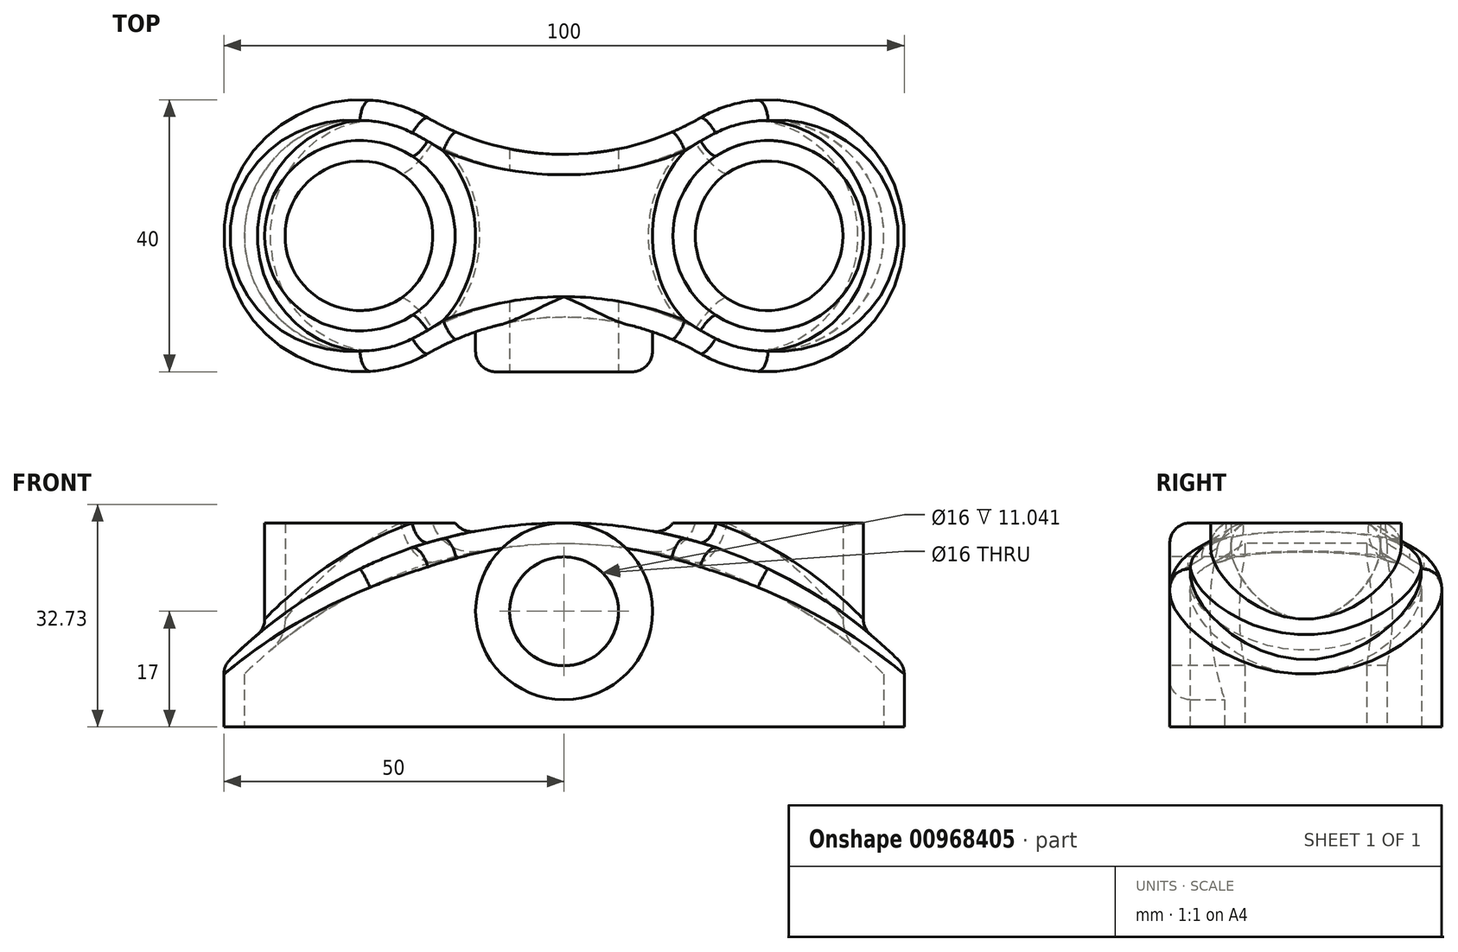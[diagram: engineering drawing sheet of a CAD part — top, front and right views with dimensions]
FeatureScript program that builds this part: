
annotation { "Feature Type Name" : "Feature", "Feature Type Description" : "" }
export const myFeature = defineFeature(function(context is Context, id is Id, definition is map)
    precondition{}
    {
        {
            var Q0;
            Q0=qCreatedBy(makeId("Top.planeOp"),FACE);
            var sketch = newSketch(context, id + "F0", { "sketchPlane" : qUnion([Q0])});
            skArc(sketch, "E0", {"start": v(-20, 17.32) * mm, "mid": v(-50, 0) * mm, "end": v(-20, -17.32) * mm});
            skArc(sketch, "E1", {"start": v(20, -17.32) * mm, "mid": v(50, 0) * mm, "end": v(20, 17.32) * mm});
            skArc(sketch, "E2", {"start": v(-20, 17.32) * mm, "mid": v(0, 11.96) * mm, "end": v(20, 17.32) * mm});
            skArc(sketch, "E3.MirrorCS", {"start": v(-20, -17.32) * mm, "mid": v(0, -11.96) * mm, "end": v(20, -17.32) * mm});
            skCircle(sketch, "E4", {"center": v(-30, 0) * mm, "radius": 11 * mm});
            skCircle(sketch, "E5", {"center": v(30, 0) * mm, "radius": 11 * mm});
            skCircle(sketch, "E6", {"center": v(-30, 0) * mm, "radius": 14 * mm});
            skCircle(sketch, "E7", {"center": v(30, 0) * mm, "radius": 14 * mm});
            skSolve(sketch);
        }
        {
            var Q0;
            Q0=qCreatedBy(makeId("Front.planeOp"),FACE);
            var sketch = newSketch(context, id + "F1", { "sketchPlane" : qUnion([Q0])});
            skCircle(sketch, "E8", {"center": v(0, 17) * mm, "radius": 13 * mm});
            skCircle(sketch, "E9", {"center": v(0, 17) * mm, "radius": 8 * mm});
            skSolve(sketch);
        }
        {
            var Q0;
            Q0=qCreatedBy(makeId("Front.planeOp"),FACE);
            var sketch = newSketch(context, id + "F2", { "sketchPlane" : qUnion([Q0])});
            skArc(sketch, "E10", {"start": v(57.45, 0) * mm, "mid": v(0, 30) * mm, "end": v(-57.45, 0) * mm});
            skSolve(sketch);
        }
        {
            var Q0;
            Q0=sQuery(id+"F2.wireOp",EDGE,"E10");
            extrude(context, id + "F3", {"bodyType" : ToolBodyType.SURFACE, "surfaceEntities" : qUnion([Q0]), "depth" : 50 * mm, "offsetDistance" : 25 * mm, "symmetric" : true});
        }
        {
            var Q0;
            Q0=makeQuery(id+"F0.imprint","IMPRINT",FACE,{"disambiguationData":[TD([[makeQuery(id+"F0.imprint","IMPRINT",EDGE,{"derivedFrom":sQuery(id+"F0.wireOp",EDGE,"E0")}),1.0]])]});
            var Q1;
            Q1=makeQuery(id+"F0.imprint","IMPRINT",FACE,{"disambiguationData":[TD([[makeQuery(id+"F0.imprint","IMPRINT",EDGE,{"derivedFrom":sQuery(id+"F0.wireOp",EDGE,"E4")}),-1.0]])]});
            var Q2;
            Q2=makeQuery(id+"F0.imprint","IMPRINT",FACE,{"disambiguationData":[TD([[makeQuery(id+"F0.imprint","IMPRINT",EDGE,{"derivedFrom":sQuery(id+"F0.wireOp",EDGE,"E4")}),1.0]])]});
            var Q3;
            Q3=makeQuery(id+"F0.imprint","IMPRINT",FACE,{"disambiguationData":[TD([[makeQuery(id+"F0.imprint","IMPRINT",EDGE,{"derivedFrom":sQuery(id+"F0.wireOp",EDGE,"E5")}),1.0]])]});
            var Q4;
            Q4=makeQuery(id+"F0.imprint","IMPRINT",FACE,{"disambiguationData":[TD([[makeQuery(id+"F0.imprint","IMPRINT",EDGE,{"derivedFrom":sQuery(id+"F0.wireOp",EDGE,"E5")}),-1.0]])]});
            var Q5;
            Q5=makeQuery(id+"F3.opExtrude","SWEPT_BODY",BODY,{"disambiguationData":[OSD([sQuery(id+"F2.wireOp",EDGE,"E10")])]});
            extrude(context, id + "F4", {"entities" : qUnion([Q0, Q1, Q2, Q3, Q4]), "endBound" : BoundingType.UP_TO_BODY, "depth" : 25 * mm, "endBoundEntityBody" : qUnion([Q5]), "offsetDistance" : 25 * mm});
        }
        {
            var Q0;
            Q0=makeQuery(id+"F0.imprint","IMPRINT",FACE,{"disambiguationData":[TD([[makeQuery(id+"F0.imprint","IMPRINT",EDGE,{"derivedFrom":sQuery(id+"F0.wireOp",EDGE,"E4")}),-1.0]])]});
            var Q1;
            Q1=makeQuery(id+"F0.imprint","IMPRINT",FACE,{"disambiguationData":[TD([[makeQuery(id+"F0.imprint","IMPRINT",EDGE,{"derivedFrom":sQuery(id+"F0.wireOp",EDGE,"E4")}),1.0]])]});
            var Q2;
            Q2=makeQuery(id+"F0.imprint","IMPRINT",FACE,{"disambiguationData":[TD([[makeQuery(id+"F0.imprint","IMPRINT",EDGE,{"derivedFrom":sQuery(id+"F0.wireOp",EDGE,"E5")}),-1.0]])]});
            var Q3;
            Q3=makeQuery(id+"F0.imprint","IMPRINT",FACE,{"disambiguationData":[TD([[makeQuery(id+"F0.imprint","IMPRINT",EDGE,{"derivedFrom":sQuery(id+"F0.wireOp",EDGE,"E5")}),1.0]])]});
            extrude(context, id + "F5", {"entities" : qUnion([Q0, Q1, Q2, Q3]), "operationType" : NewBodyOperationType.ADD, "depth" : 30 * mm, "offsetDistance" : 25 * mm});
        }
        {
            var Q0;
            Q0=makeQuery(id+"F5.boolean.opBoolean","INTERSECT",EDGE,{"derivedFrom":[makeQuery(id+"F4.opExtrude","CAP_FACE",FACE,{"disambiguationData":[OSD([sQuery(id+"F0.wireOp",EDGE,"E0"),sQuery(id+"F0.wireOp",EDGE,"E1"),sQuery(id+"F0.wireOp",EDGE,"E2"),sQuery(id+"F0.wireOp",EDGE,"E3.MirrorCS")])],"isStart":false}),makeQuery(id+"F5.opExtrude","SWEPT_FACE",FACE,{"disambiguationData":[OSD([sQuery(id+"F0.wireOp",EDGE,"E6")])]})]});
            var Q1;
            Q1=makeQuery(id+"F5.boolean.opBoolean","INTERSECT",EDGE,{"derivedFrom":[makeQuery(id+"F4.opExtrude","CAP_FACE",FACE,{"disambiguationData":[OSD([sQuery(id+"F0.wireOp",EDGE,"E0"),sQuery(id+"F0.wireOp",EDGE,"E1"),sQuery(id+"F0.wireOp",EDGE,"E2"),sQuery(id+"F0.wireOp",EDGE,"E3.MirrorCS")])],"isStart":false}),makeQuery(id+"F5.opExtrude","SWEPT_FACE",FACE,{"disambiguationData":[OSD([sQuery(id+"F0.wireOp",EDGE,"E7")])]})]});
            fillet(context, id + "F6", {"entities" : qUnion([Q0, Q1]), "tangentPropagation" : true, "radius" : 3 * mm, "defaultsChanged" : false, "vertexSettings" : [], "allowEdgeOverflow" : false});
        }
        {
            var Q0;
            Q0=makeQuery(id+"F4.opExtrude","CAP_EDGE",EDGE,{"disambiguationData":[OSD([sQuery(id+"F0.wireOp",EDGE,"E0")])],"isStart":false});
            fillet(context, id + "F7", {"entities" : qUnion([Q0]), "tangentPropagation" : true, "radius" : 3 * mm, "defaultsChanged" : false, "vertexSettings" : [], "allowEdgeOverflow" : false});
        }
        {
            var Q0;
            Q0=makeQuery(id+"F5.opExtrude","CAP_FACE",FACE,{"disambiguationData":[OSD([sQuery(id+"F0.wireOp",EDGE,"E6")])],"isStart":false});
            var Q1;
            Q1=makeQuery(id+"F5.opExtrude","CAP_FACE",FACE,{"disambiguationData":[OSD([sQuery(id+"F0.wireOp",EDGE,"E7")])],"isStart":false});
            var Q2;
            Q2=makeQuery(id+"F4.opExtrude","CAP_FACE",FACE,{"disambiguationData":[OSD([sQuery(id+"F0.wireOp",EDGE,"E0"),sQuery(id+"F0.wireOp",EDGE,"E1"),sQuery(id+"F0.wireOp",EDGE,"E2"),sQuery(id+"F0.wireOp",EDGE,"E3.MirrorCS")])],"isStart":true});
            shell(context, id + "F8", {"entities" : qUnion([Q0, Q1, Q2]), "thickness" : 3 * mm});
        }
        {
            var Q0;
            Q0=makeQuery(id+"F1.imprint","IMPRINT",FACE,{"disambiguationData":[TD([[makeQuery(id+"F1.imprint","IMPRINT",EDGE,{"derivedFrom":sQuery(id+"F1.wireOp",EDGE,"E8")}),1.0]])]});
            var Q1;
            Q1=makeQuery(id+"F1.imprint","IMPRINT",FACE,{"disambiguationData":[TD([[makeQuery(id+"F1.imprint","IMPRINT",EDGE,{"derivedFrom":sQuery(id+"F1.wireOp",EDGE,"E9")}),1.0]])]});
            var Q2;
            Q2=makeQuery(id+"F4.opExtrude","SWEPT_BODY",BODY,{"disambiguationData":[OSD([sQuery(id+"F0.wireOp",EDGE,"E0"),sQuery(id+"F0.wireOp",EDGE,"E1"),sQuery(id+"F0.wireOp",EDGE,"E2"),sQuery(id+"F0.wireOp",EDGE,"E3.MirrorCS")])]});
            extrude(context, id + "F9", {"entities" : qUnion([Q0, Q1]), "operationType" : NewBodyOperationType.ADD, "depth" : 20 * mm, "offsetDistance" : 25 * mm, "hasSecondDirection" : true, "secondDirectionBound" : BoundingType.UP_TO_BODY, "secondDirectionOppositeDirection" : false, "secondDirectionDepth" : 25 * mm, "secondDirectionBoundEntityBody" : qUnion([Q2])});
        }
        {
            var Q0;
            Q0=makeQuery(id+"F9.opExtrude","CAP_EDGE",EDGE,{"disambiguationData":[OSD([sQuery(id+"F1.wireOp",EDGE,"E8")]),topologyDisambiguationEdgeConnected([makeQuery(id+"F4.opExtrude","SWEPT_FACE",FACE,{"disambiguationData":[OSD([sQuery(id+"F0.wireOp",EDGE,"E3.MirrorCS")])]})])],"isStart":false});
            var Q1;
            Q1=makeQuery(id+"F49KFklj5Yib0Bw_2.1.F9.opExtrude","CAP_EDGE",EDGE,{"disambiguationData":[OSD([sQuery(id+"F1.wireOp",EDGE,"E8")]),topologyDisambiguationEdgeConnected([makeQuery(id+"F4.opExtrude","SWEPT_FACE",FACE,{"disambiguationData":[OSD([sQuery(id+"F0.wireOp",EDGE,"E2")])]})])],"isStart":false});
            fillet(context, id + "F10", {"entities" : qUnion([Q0, Q1]), "tangentPropagation" : true, "radius" : 3 * mm, "defaultsChanged" : false, "vertexSettings" : [], "allowEdgeOverflow" : false});
        }
        {
            var Q0;
            Q0=makeQuery(id+"F1.imprint","IMPRINT",FACE,{"disambiguationData":[TD([[makeQuery(id+"F1.imprint","IMPRINT",EDGE,{"derivedFrom":sQuery(id+"F1.wireOp",EDGE,"E9")}),1.0]])]});
            extrude(context, id + "F11", {"entities" : qUnion([Q0]), "operationType" : NewBodyOperationType.REMOVE, "oppositeDirection" : true, "depth" : 75 * mm, "offsetDistance" : 25 * mm, "symmetric" : true});
        }
    });
